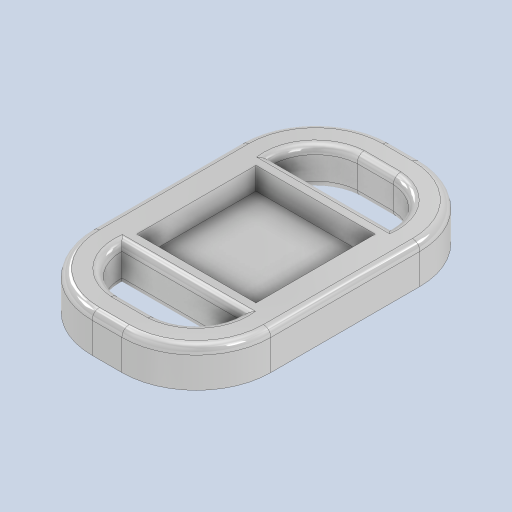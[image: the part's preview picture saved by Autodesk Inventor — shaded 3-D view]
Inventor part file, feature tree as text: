
AUTODESK INVENTOR PART (.ipt)
format: ipt  version: 2024 (Build 280153000, 153)  size: 252,416 bytes
history: native  units: mm
features: other x2, extrude x2, sketch x2, fillet x1
ambient origin geometry x8: Origin, YZ Plane, XZ Plane, XY Plane, X Axis, Y Axis, Z Axis, Center Point
bodies: Body1 (feature_tree)
feature tree (7):
  other  "Sólido1"
  extrude  "Extrusión1"  Depth=50.0mm
  extrude  "Extrusión2"  Depth=5.0mm
  fillet  "Empalme1"  Radius=30.0mm
  sketch  "Boceto1"  dims[d0=120.0mm d2=50.0mm]
  sketch  "Boceto2"  dims[d3=200.0mm d5=80.0mm d6=30.0mm d7=25.4mm d8=0.0mm d9=10.0mm d10=15.0mm d11=0.0mm d12=5.0mm]
  other  "Proyectar aristas de corte1"
